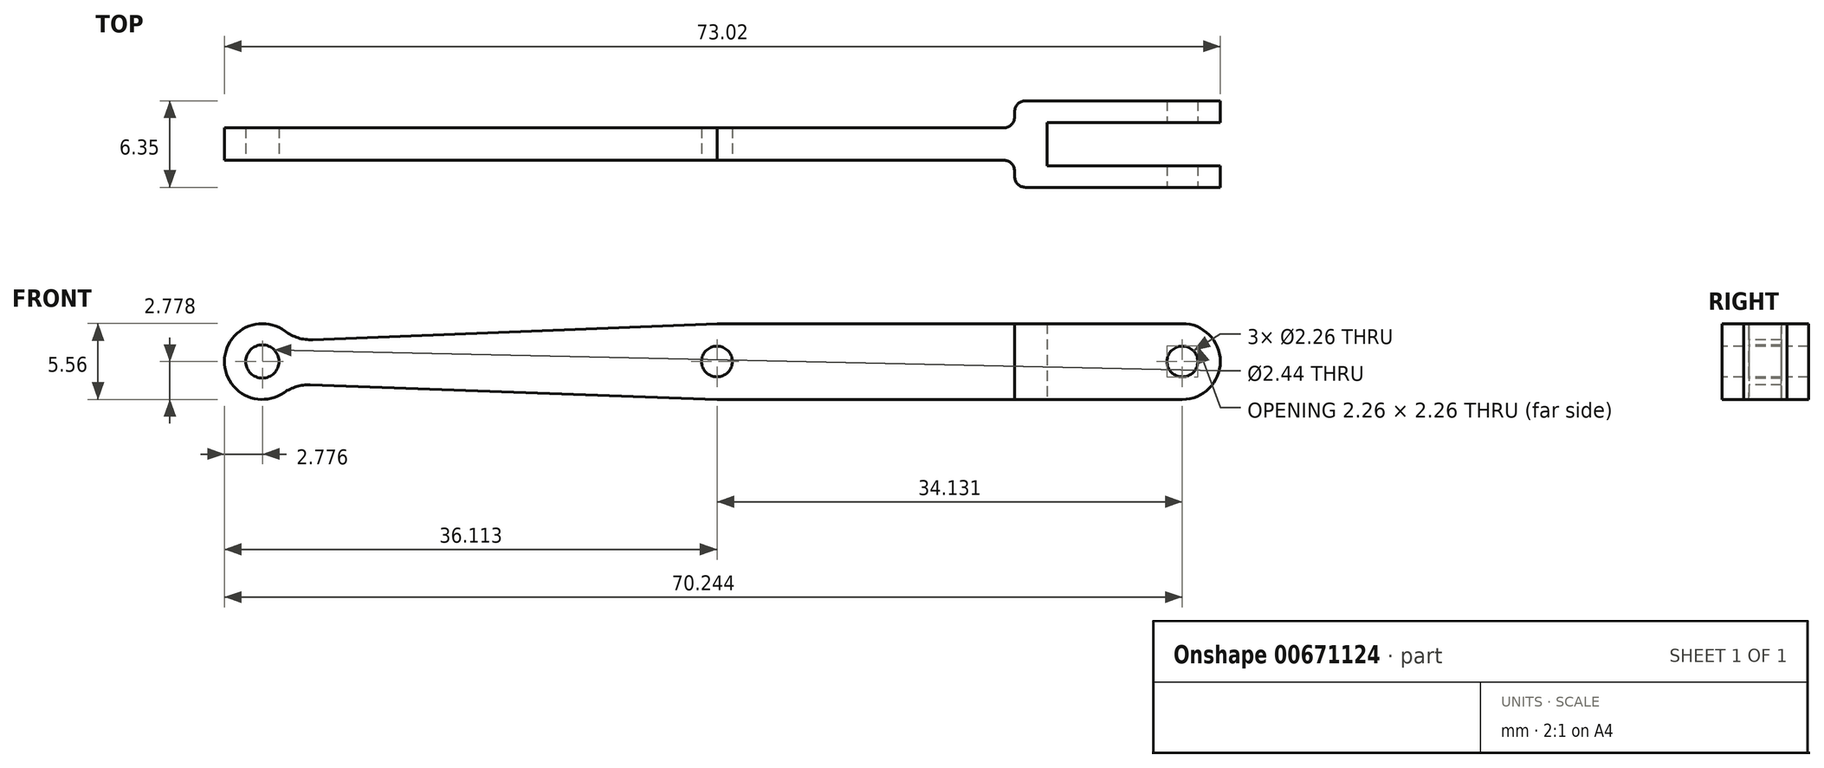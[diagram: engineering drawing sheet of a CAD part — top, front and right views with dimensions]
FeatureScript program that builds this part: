
annotation { "Feature Type Name" : "Feature", "Feature Type Description" : "" }
export const myFeature = defineFeature(function(context is Context, id is Id, definition is map)
    precondition{}
    {
        {
            var Q0;
            Q0=qCreatedBy(makeId("Top.planeOp"),FACE);
            var sketch = newSketch(context, id + "F0", { "sketchPlane" : qUnion([Q0])});
            skLineSegment(sketch, "E0", {"start": v(-28.05, 23.01) * mm, "end": v(29.1, 23.01) * mm});
            skLineSegment(sketch, "E1", {"start": v(29.9, 23.8) * mm, "end": v(29.9, 24.2) * mm});
            skLineSegment(sketch, "E2", {"start": v(30.68, 25) * mm, "end": v(44.97, 25) * mm});
            skLineSegment(sketch, "E3", {"start": v(44.97, 25) * mm, "end": v(44.97, 23.4) * mm});
            skLineSegment(sketch, "E4", {"start": v(44.97, 23.4) * mm, "end": v(32.27, 23.4) * mm});
            skLineSegment(sketch, "E5", {"start": v(32.27, 23.4) * mm, "end": v(32.27, 20.23) * mm});
            skLineSegment(sketch, "E6", {"start": v(32.27, 20.23) * mm, "end": v(44.97, 20.23) * mm});
            skLineSegment(sketch, "E7", {"start": v(44.97, 20.23) * mm, "end": v(44.97, 18.65) * mm});
            skLineSegment(sketch, "E8", {"start": v(44.97, 18.65) * mm, "end": v(30.68, 18.65) * mm});
            skLineSegment(sketch, "E9", {"start": v(29.9, 19.44) * mm, "end": v(29.9, 19.84) * mm});
            skLineSegment(sketch, "E10", {"start": v(29.1, 20.63) * mm, "end": v(-28.05, 20.63) * mm});
            skLineSegment(sketch, "E11", {"start": v(-28.05, 20.63) * mm, "end": v(-28.05, 23.01) * mm});
            skPoint(sketch, "E12.visualSharp", {"position": v(29.9, 23.01) * mm});
            skArc(sketch, "E12.filletArc", {"start": v(29.1, 23.01) * mm, "mid": v(29.66, 23.25) * mm, "end": v(29.9, 23.8) * mm});
            skPoint(sketch, "E13.visualSharp", {"position": v(29.9, 25) * mm});
            skArc(sketch, "E13.filletArc", {"start": v(30.68, 25) * mm, "mid": v(30.12, 24.76) * mm, "end": v(29.9, 24.2) * mm});
            skPoint(sketch, "E14.visualSharp", {"position": v(29.9, 20.63) * mm});
            skArc(sketch, "E14.filletArc", {"start": v(29.9, 19.84) * mm, "mid": v(29.66, 20.4) * mm, "end": v(29.1, 20.63) * mm});
            skPoint(sketch, "E15.visualSharp", {"position": v(29.9, 18.65) * mm});
            skArc(sketch, "E15.filletArc", {"start": v(29.9, 19.44) * mm, "mid": v(30.12, 18.88) * mm, "end": v(30.68, 18.65) * mm});
            skSolve(sketch);
        }
        {
            var Q0;
            Q0=qSketchRegion(id+"F0",true);
            extrude(context, id + "F1", {"entities" : qUnion([Q0]), "depth" : 5.56 * mm});
        }
        {
            var Q0;
            Q0=makeQuery(id+"F1.opExtrude","SWEPT_FACE",FACE,{"disambiguationData":[OSD([sQuery(id+"F0.wireOp",EDGE,"E10")])]});
            var sketch = newSketch(context, id + "F2", { "sketchPlane" : qUnion([Q0])});
            skCircle(sketch, "E16", {"center": v(-25.27, 2.78) * mm, "radius": 1.22 * mm});
            skSolve(sketch);
        }
        {
            var Q0;
            Q0=qSketchRegion(id+"F2",true);
            extrude(context, id + "F3", {"entities" : qUnion([Q0]), "operationType" : NewBodyOperationType.REMOVE, "oppositeDirection" : true, "depth" : 25.4 * mm});
        }
        {
            var Q0;
            Q0=makeQuery(id+"F1.opExtrude","SWEPT_FACE",FACE,{"disambiguationData":[OSD([sQuery(id+"F0.wireOp",EDGE,"E8")])]});
            var sketch = newSketch(context, id + "F4", { "sketchPlane" : qUnion([Q0])});
            skCircle(sketch, "E17", {"center": v(42.2, 2.78) * mm, "radius": 1.13 * mm});
            skSolve(sketch);
        }
        {
            var Q0;
            Q0=qSketchRegion(id+"F4",true);
            extrude(context, id + "F5", {"entities" : qUnion([Q0]), "operationType" : NewBodyOperationType.REMOVE, "oppositeDirection" : true, "depth" : 25.4 * mm});
        }
        {
            var Q0;
            Q0=makeQuery(id+"F1.opExtrude","CAP_EDGE",EDGE,{"disambiguationData":[OSD([sQuery(id+"F0.wireOp",EDGE,"E7")])],"isStart":false});
            var Q1;
            Q1=makeQuery(id+"F1.opExtrude","CAP_EDGE",EDGE,{"disambiguationData":[OSD([sQuery(id+"F0.wireOp",EDGE,"E7")])],"isStart":true});
            var Q2;
            Q2=makeQuery(id+"F1.opExtrude","CAP_EDGE",EDGE,{"disambiguationData":[OSD([sQuery(id+"F0.wireOp",EDGE,"E3")])],"isStart":true});
            var Q3;
            Q3=makeQuery(id+"F1.opExtrude","CAP_EDGE",EDGE,{"disambiguationData":[OSD([sQuery(id+"F0.wireOp",EDGE,"E3")])],"isStart":false});
            fillet(context, id + "F6", {"entities" : qUnion([Q0, Q1, Q2, Q3]), "radius" : 2.78 * mm, "tangentPropagation" : true, "allowEdgeOverflow" : false});
        }
        {
            var Q0;
            Q0=makeQuery(id+"F1.opExtrude","CAP_EDGE",EDGE,{"disambiguationData":[OSD([sQuery(id+"F0.wireOp",EDGE,"E11")])],"isStart":false});
            var Q1;
            Q1=makeQuery(id+"F1.opExtrude","CAP_EDGE",EDGE,{"disambiguationData":[OSD([sQuery(id+"F0.wireOp",EDGE,"E11")])],"isStart":true});
            fillet(context, id + "F7", {"entities" : qUnion([Q0, Q1]), "radius" : 2.78 * mm, "tangentPropagation" : true, "allowEdgeOverflow" : false});
        }
        {
            var Q0;
            Q0=makeQuery(id+"F1.opExtrude","SWEPT_FACE",FACE,{"disambiguationData":[OSD([sQuery(id+"F0.wireOp",EDGE,"E10")])]});
            var sketch = newSketch(context, id + "F8", { "sketchPlane" : qUnion([Q0])});
            skCircle(sketch, "E18", {"center": v(8.06, 2.78) * mm, "radius": 1.13 * mm});
            skArc(sketch, "E19", {"start": v(-25.27, 0) * mm, "mid": v(-22.5, 2.78) * mm, "end": v(-25.27, 5.56) * mm});
            skPoint(sketch, "E20", {"position": v(8.06, 5.56) * mm});
            skPoint(sketch, "E21", {"position": v(8.06, 0) * mm});
            skLineSegment(sketch, "E22", {"start": v(-22.96, 4.32) * mm, "end": v(8.06, 5.56) * mm});
            skLineSegment(sketch, "E23", {"start": v(-23.05, 1.11) * mm, "end": v(8.06, 0) * mm});
            skArc(sketch, "E24", {"start": v(-23.61, 5) * mm, "mid": v(-22.65, 4.52) * mm, "end": v(-21.59, 4.38) * mm});
            skArc(sketch, "E25", {"start": v(-21.76, 1.07) * mm, "mid": v(-22.77, 0.94) * mm, "end": v(-23.69, 0.5) * mm});
            skSolve(sketch);
        }
        {
            var Q0;
            Q0=makeQuery(id+"F8.imprint","IMPRINT",FACE,{"disambiguationData":[TD([[makeQuery(id+"F8.imprint","IMPRINT",EDGE,{"derivedFrom":sQuery(id+"F8.wireOp",EDGE,"E18")}),1.0]])]});
            var Q1;
            {var subQ4=sQuery(id+"F8.wireOp",EDGE,"E24");Q1=makeQuery(id+"F8.imprint","IMPRINT",FACE,{"disambiguationData":[TD([[makeQuery(id+"F8.imprint","IMPRINT",EDGE,{"derivedFrom":subQ4}),1.0]])]});}
            var Q2;
            {var subQ4=sQuery(id+"F8.wireOp",EDGE,"E25");Q2=makeQuery(id+"F8.imprint","IMPRINT",FACE,{"disambiguationData":[TD([[makeQuery(id+"F8.imprint","IMPRINT",EDGE,{"derivedFrom":subQ4}),1.0]])]});}
            extrude(context, id + "F9", {"entities" : qUnion([Q0, Q1, Q2]), "operationType" : NewBodyOperationType.REMOVE, "oppositeDirection" : true, "depth" : 25.4 * mm});
        }
    });
